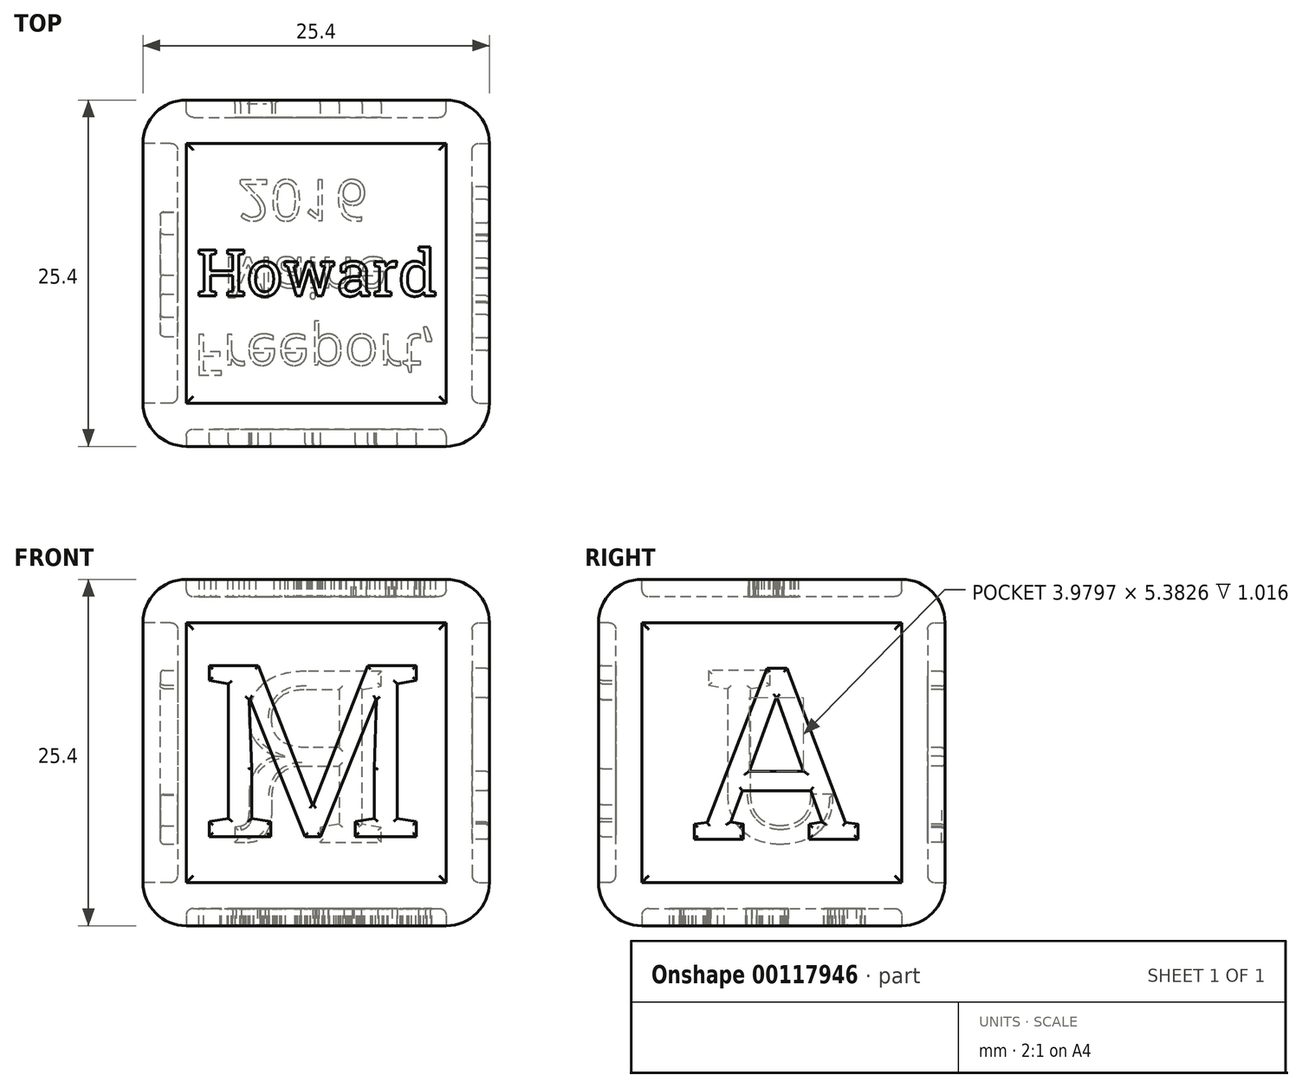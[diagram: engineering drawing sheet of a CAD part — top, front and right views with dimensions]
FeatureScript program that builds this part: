
annotation { "Feature Type Name" : "Feature", "Feature Type Description" : "" }
export const myFeature = defineFeature(function(context is Context, id is Id, definition is map)
    precondition{}
    {
        {
            var Q0;
            Q0=qCreatedBy(makeId("Top.planeOp"),FACE);
            var sketch = newSketch(context, id + "F0", { "sketchPlane" : qUnion([Q0])});
            skLineSegment(sketch, "E0.bottom", {"start": v(12.7, -12.7) * mm, "end": v(-12.7, -12.7) * mm});
            skLineSegment(sketch, "E0.top", {"start": v(12.7, 12.7) * mm, "end": v(-12.7, 12.7) * mm});
            skLineSegment(sketch, "E0.left", {"start": v(12.7, -12.7) * mm, "end": v(12.7, 12.7) * mm});
            skLineSegment(sketch, "E0.right", {"start": v(-12.7, -12.7) * mm, "end": v(-12.7, 12.7) * mm});
            skPoint(sketch, "E0.middle", {"position": v(0, 0) * mm});
            skSolve(sketch);
        }
        {
            var Q0;
            Q0=makeQuery(id+"F0.imprint","IMPRINT",FACE,{"disambiguationData":[TD([[makeQuery(id+"F0.imprint","IMPRINT",EDGE,{"derivedFrom":sQuery(id+"F0.wireOp",EDGE,"E0.bottom")}),-1.0]])]});
            extrude(context, id + "F1", {"entities" : qUnion([Q0]), "depth" : 25.4 * mm});
        }
        {
            var Q0;
            Q0=makeQuery(id+"F1.opExtrude","CAP_FACE",FACE,{"disambiguationData":[OSD([sQuery(id+"F0.wireOp",EDGE,"E0.bottom"),sQuery(id+"F0.wireOp",EDGE,"E0.top"),sQuery(id+"F0.wireOp",EDGE,"E0.left"),sQuery(id+"F0.wireOp",EDGE,"E0.right")])],"isStart":false});
            var Q1;
            Q1=makeQuery(id+"F1.opExtrude","SWEPT_FACE",FACE,{"disambiguationData":[OSD([sQuery(id+"F0.wireOp",EDGE,"E0.bottom")])]});
            var Q2;
            Q2=makeQuery(id+"F1.opExtrude","SWEPT_FACE",FACE,{"disambiguationData":[OSD([sQuery(id+"F0.wireOp",EDGE,"E0.left")])]});
            var Q3;
            Q3=makeQuery(id+"F1.opExtrude","CAP_FACE",FACE,{"disambiguationData":[OSD([sQuery(id+"F0.wireOp",EDGE,"E0.bottom"),sQuery(id+"F0.wireOp",EDGE,"E0.top"),sQuery(id+"F0.wireOp",EDGE,"E0.left"),sQuery(id+"F0.wireOp",EDGE,"E0.right")])],"isStart":true});
            var Q4;
            Q4=makeQuery(id+"F1.opExtrude","SWEPT_FACE",FACE,{"disambiguationData":[OSD([sQuery(id+"F0.wireOp",EDGE,"E0.right")])]});
            fillet(context, id + "F2", {"entities" : qUnion([Q0, Q1, Q2, Q3, Q4]), "radius" : 3.17 * mm, "tangentPropagation" : true, "allowEdgeOverflow" : false});
        }
        {
            var Q0;
            Q0=makeQuery(id+"F1.opExtrude","SWEPT_FACE",FACE,{"disambiguationData":[OSD([sQuery(id+"F0.wireOp",EDGE,"E0.bottom")])]});
            var sketch = newSketch(context, id + "F3", { "sketchPlane" : qUnion([Q0])});
            skPoint(sketch, "E1", {"position": v(0, 22.23) * mm});
            skLineSegment(sketch, "E2", {"start": v(0, 22.23) * mm, "end": v(0, 3.18) * mm, "construction": true});
            skLineSegment(sketch, "E3", {"start": v(9.53, 12.7) * mm, "end": v(-9.53, 12.7) * mm, "construction": true});
            skPoint(sketch, "E4", {"position": v(0, 12.7) * mm});
            skSolve(sketch);
        }
        {
            var Q0;
            {var subQ0=sQuery(id+"F0.wireOp",EDGE,"E0.bottom");var subQ1=makeQuery(id+"F1.opExtrude","SWEPT_FACE",FACE,{"disambiguationData":[OSD([subQ0])]});Q0=makeQuery(id+"F3.imprint","IMPRINT",FACE,{"disambiguationData":[TD([[makeQuery(id+"F3.imprint","IMPRINT",EDGE,{"derivedFrom":makeQuery(id+"F2.opFillet","BLEND_EDGE",EDGE,{"blendedFrom":[makeQuery(id+"F1.opExtrude","CAP_EDGE",EDGE,{"disambiguationData":[OSD([subQ0])],"isStart":true}),subQ1],"blendedInto":[subQ1]})}),1.0]])]});}
            extrude(context, id + "F4", {"entities" : qUnion([Q0]), "operationType" : NewBodyOperationType.REMOVE, "oppositeDirection" : true, "depth" : 1.27 * mm});
        }
        {
            var Q0;
            Q0=makeQuery(id+"F1.opExtrude","SWEPT_FACE",FACE,{"disambiguationData":[OSD([sQuery(id+"F0.wireOp",EDGE,"E0.left")])]});
            extrude(context, id + "F5", {"entities" : qUnion([Q0]), "operationType" : NewBodyOperationType.REMOVE, "oppositeDirection" : true, "depth" : 1.27 * mm});
        }
        {
            var Q0;
            Q0=makeQuery(id+"F1.opExtrude","SWEPT_FACE",FACE,{"disambiguationData":[OSD([sQuery(id+"F0.wireOp",EDGE,"E0.right")])]});
            extrude(context, id + "F6", {"entities" : qUnion([Q0]), "operationType" : NewBodyOperationType.REMOVE, "oppositeDirection" : true, "depth" : 2.54 * mm});
        }
        {
            var Q0;
            Q0=makeQuery(id+"F1.opExtrude","SWEPT_FACE",FACE,{"disambiguationData":[OSD([sQuery(id+"F0.wireOp",EDGE,"E0.top")])]});
            extrude(context, id + "F7", {"entities" : qUnion([Q0]), "operationType" : NewBodyOperationType.REMOVE, "oppositeDirection" : true, "depth" : 1.27 * mm});
        }
        {
            var Q0;
            Q0=makeQuery(id+"F1.opExtrude","CAP_FACE",FACE,{"disambiguationData":[OSD([sQuery(id+"F0.wireOp",EDGE,"E0.bottom"),sQuery(id+"F0.wireOp",EDGE,"E0.top"),sQuery(id+"F0.wireOp",EDGE,"E0.left"),sQuery(id+"F0.wireOp",EDGE,"E0.right")])],"isStart":true});
            extrude(context, id + "F8", {"entities" : qUnion([Q0]), "operationType" : NewBodyOperationType.REMOVE, "oppositeDirection" : true, "depth" : 1.27 * mm});
        }
        {
            var Q0;
            Q0=makeQuery(id+"F1.opExtrude","CAP_FACE",FACE,{"disambiguationData":[OSD([sQuery(id+"F0.wireOp",EDGE,"E0.bottom"),sQuery(id+"F0.wireOp",EDGE,"E0.top"),sQuery(id+"F0.wireOp",EDGE,"E0.left"),sQuery(id+"F0.wireOp",EDGE,"E0.right")])],"isStart":false});
            extrude(context, id + "F9", {"entities" : qUnion([Q0]), "operationType" : NewBodyOperationType.REMOVE, "oppositeDirection" : true, "depth" : 1.27 * mm});
        }
        {
            var Q0;
            {var subQ0=sQuery(id+"F0.wireOp",EDGE,"E0.right");Q0=makeQuery(id+"F6.boolean.opBoolean","COPY",EDGE,{"derivedFrom":makeQuery(id+"F6.opExtrude","CAP_EDGE",EDGE,{"disambiguationData":[OSD([subQ0]),TDD([makeQuery(id+"F2.opFillet","BLEND_EDGE",EDGE,{"blendedFrom":[makeQuery(id+"F1.opExtrude","CAP_EDGE",EDGE,{"disambiguationData":[OSD([subQ0])],"isStart":true}),makeQuery(id+"F1.opExtrude","SWEPT_FACE",FACE,{"disambiguationData":[OSD([subQ0])]})],"blendedInto":[makeQuery(id+"F1.opExtrude","SWEPT_FACE",FACE,{"disambiguationData":[OSD([subQ0])]})]})])],"isStart":false})});}
            var Q1;
            Q1=makeQuery(id+"F6.boolean.opBoolean","COPY",EDGE,{"derivedFrom":makeQuery(id+"F6.opExtrude","CAP_EDGE",EDGE,{"disambiguationData":[OSD([sQuery(id+"F0.wireOp",EDGE,"E0.bottom"),sQuery(id+"F0.wireOp",EDGE,"E0.right")])],"isStart":false})});
            var Q2;
            {var subQ0=sQuery(id+"F0.wireOp",EDGE,"E0.right");Q2=makeQuery(id+"F6.boolean.opBoolean","COPY",EDGE,{"derivedFrom":makeQuery(id+"F6.opExtrude","CAP_EDGE",EDGE,{"disambiguationData":[OSD([subQ0]),TDD([makeQuery(id+"F2.opFillet","BLEND_EDGE",EDGE,{"blendedFrom":[makeQuery(id+"F1.opExtrude","CAP_EDGE",EDGE,{"disambiguationData":[OSD([subQ0])],"isStart":false}),makeQuery(id+"F1.opExtrude","SWEPT_FACE",FACE,{"disambiguationData":[OSD([subQ0])]})],"blendedInto":[makeQuery(id+"F1.opExtrude","SWEPT_FACE",FACE,{"disambiguationData":[OSD([subQ0])]})]})])],"isStart":false})});}
            var Q3;
            Q3=makeQuery(id+"F6.boolean.opBoolean","COPY",EDGE,{"derivedFrom":makeQuery(id+"F6.opExtrude","CAP_EDGE",EDGE,{"disambiguationData":[OSD([sQuery(id+"F0.wireOp",EDGE,"E0.top"),sQuery(id+"F0.wireOp",EDGE,"E0.right")])],"isStart":false})});
            var Q4;
            Q4=makeQuery(id+"F4.boolean.opBoolean","COPY",EDGE,{"derivedFrom":makeQuery(id+"F4.opExtrude","CAP_EDGE",EDGE,{"disambiguationData":[OSD([sQuery(id+"F0.wireOp",EDGE,"E0.bottom"),sQuery(id+"F0.wireOp",EDGE,"E0.right")])],"isStart":false})});
            var Q5;
            {var subQ0=sQuery(id+"F0.wireOp",EDGE,"E0.bottom");Q5=makeQuery(id+"F4.boolean.opBoolean","COPY",EDGE,{"derivedFrom":makeQuery(id+"F4.opExtrude","CAP_EDGE",EDGE,{"disambiguationData":[OSD([subQ0]),TDD([makeQuery(id+"F3.imprint","IMPRINT",EDGE,{"derivedFrom":makeQuery(id+"F2.opFillet","BLEND_EDGE",EDGE,{"blendedFrom":[makeQuery(id+"F1.opExtrude","CAP_EDGE",EDGE,{"disambiguationData":[OSD([subQ0])],"isStart":true}),makeQuery(id+"F1.opExtrude","SWEPT_FACE",FACE,{"disambiguationData":[OSD([subQ0])]})],"blendedInto":[makeQuery(id+"F1.opExtrude","SWEPT_FACE",FACE,{"disambiguationData":[OSD([subQ0])]})]})})])],"isStart":false})});}
            var Q6;
            {var subQ0=sQuery(id+"F0.wireOp",EDGE,"E0.bottom");Q6=makeQuery(id+"F4.boolean.opBoolean","COPY",EDGE,{"derivedFrom":makeQuery(id+"F4.opExtrude","CAP_EDGE",EDGE,{"disambiguationData":[OSD([subQ0]),TDD([makeQuery(id+"F3.imprint","IMPRINT",EDGE,{"derivedFrom":makeQuery(id+"F2.opFillet","BLEND_EDGE",EDGE,{"blendedFrom":[makeQuery(id+"F1.opExtrude","CAP_EDGE",EDGE,{"disambiguationData":[OSD([subQ0])],"isStart":false}),makeQuery(id+"F1.opExtrude","SWEPT_FACE",FACE,{"disambiguationData":[OSD([subQ0])]})],"blendedInto":[makeQuery(id+"F1.opExtrude","SWEPT_FACE",FACE,{"disambiguationData":[OSD([subQ0])]})]})})])],"isStart":false})});}
            var Q7;
            Q7=makeQuery(id+"F4.boolean.opBoolean","COPY",EDGE,{"derivedFrom":makeQuery(id+"F4.opExtrude","CAP_EDGE",EDGE,{"disambiguationData":[OSD([sQuery(id+"F0.wireOp",EDGE,"E0.bottom"),sQuery(id+"F0.wireOp",EDGE,"E0.left")])],"isStart":false})});
            var Q8;
            {var subQ0=sQuery(id+"F0.wireOp",EDGE,"E0.left");Q8=makeQuery(id+"F5.boolean.opBoolean","COPY",EDGE,{"derivedFrom":makeQuery(id+"F5.opExtrude","CAP_EDGE",EDGE,{"disambiguationData":[OSD([subQ0]),TDD([makeQuery(id+"F2.opFillet","BLEND_EDGE",EDGE,{"blendedFrom":[makeQuery(id+"F1.opExtrude","CAP_EDGE",EDGE,{"disambiguationData":[OSD([subQ0])],"isStart":false}),makeQuery(id+"F1.opExtrude","SWEPT_FACE",FACE,{"disambiguationData":[OSD([subQ0])]})],"blendedInto":[makeQuery(id+"F1.opExtrude","SWEPT_FACE",FACE,{"disambiguationData":[OSD([subQ0])]})]})])],"isStart":false})});}
            var Q9;
            Q9=makeQuery(id+"F5.boolean.opBoolean","COPY",EDGE,{"derivedFrom":makeQuery(id+"F5.opExtrude","CAP_EDGE",EDGE,{"disambiguationData":[OSD([sQuery(id+"F0.wireOp",EDGE,"E0.top"),sQuery(id+"F0.wireOp",EDGE,"E0.left")])],"isStart":false})});
            var Q10;
            Q10=makeQuery(id+"F5.boolean.opBoolean","COPY",EDGE,{"derivedFrom":makeQuery(id+"F5.opExtrude","CAP_EDGE",EDGE,{"disambiguationData":[OSD([sQuery(id+"F0.wireOp",EDGE,"E0.bottom"),sQuery(id+"F0.wireOp",EDGE,"E0.left")])],"isStart":false})});
            var Q11;
            {var subQ0=sQuery(id+"F0.wireOp",EDGE,"E0.left");Q11=makeQuery(id+"F5.boolean.opBoolean","COPY",EDGE,{"derivedFrom":makeQuery(id+"F5.opExtrude","CAP_EDGE",EDGE,{"disambiguationData":[OSD([subQ0]),TDD([makeQuery(id+"F2.opFillet","BLEND_EDGE",EDGE,{"blendedFrom":[makeQuery(id+"F1.opExtrude","CAP_EDGE",EDGE,{"disambiguationData":[OSD([subQ0])],"isStart":true}),makeQuery(id+"F1.opExtrude","SWEPT_FACE",FACE,{"disambiguationData":[OSD([subQ0])]})],"blendedInto":[makeQuery(id+"F1.opExtrude","SWEPT_FACE",FACE,{"disambiguationData":[OSD([subQ0])]})]})])],"isStart":false})});}
            var Q12;
            {var subQ0=sQuery(id+"F0.wireOp",EDGE,"E0.top");Q12=makeQuery(id+"F7.boolean.opBoolean","COPY",EDGE,{"derivedFrom":makeQuery(id+"F7.opExtrude","CAP_EDGE",EDGE,{"disambiguationData":[OSD([subQ0]),TDD([makeQuery(id+"F2.opFillet","BLEND_EDGE",EDGE,{"blendedFrom":[makeQuery(id+"F1.opExtrude","CAP_EDGE",EDGE,{"disambiguationData":[OSD([subQ0])],"isStart":true}),makeQuery(id+"F1.opExtrude","SWEPT_FACE",FACE,{"disambiguationData":[OSD([subQ0])]})],"blendedInto":[makeQuery(id+"F1.opExtrude","SWEPT_FACE",FACE,{"disambiguationData":[OSD([subQ0])]})]})])],"isStart":false})});}
            var Q13;
            Q13=makeQuery(id+"F7.boolean.opBoolean","COPY",EDGE,{"derivedFrom":makeQuery(id+"F7.opExtrude","CAP_EDGE",EDGE,{"disambiguationData":[OSD([sQuery(id+"F0.wireOp",EDGE,"E0.top"),sQuery(id+"F0.wireOp",EDGE,"E0.right")])],"isStart":false})});
            var Q14;
            {var subQ0=sQuery(id+"F0.wireOp",EDGE,"E0.top");Q14=makeQuery(id+"F7.boolean.opBoolean","COPY",EDGE,{"derivedFrom":makeQuery(id+"F7.opExtrude","CAP_EDGE",EDGE,{"disambiguationData":[OSD([subQ0]),TDD([makeQuery(id+"F2.opFillet","BLEND_EDGE",EDGE,{"blendedFrom":[makeQuery(id+"F1.opExtrude","CAP_EDGE",EDGE,{"disambiguationData":[OSD([subQ0])],"isStart":false}),makeQuery(id+"F1.opExtrude","SWEPT_FACE",FACE,{"disambiguationData":[OSD([subQ0])]})],"blendedInto":[makeQuery(id+"F1.opExtrude","SWEPT_FACE",FACE,{"disambiguationData":[OSD([subQ0])]})]})])],"isStart":false})});}
            var Q15;
            Q15=makeQuery(id+"F7.boolean.opBoolean","COPY",EDGE,{"derivedFrom":makeQuery(id+"F7.opExtrude","CAP_EDGE",EDGE,{"disambiguationData":[OSD([sQuery(id+"F0.wireOp",EDGE,"E0.top"),sQuery(id+"F0.wireOp",EDGE,"E0.left")])],"isStart":false})});
            var Q16;
            {var subQ0=sQuery(id+"F0.wireOp",EDGE,"E0.right");var subQ1=sQuery(id+"F0.wireOp",EDGE,"E0.left");var subQ2=sQuery(id+"F0.wireOp",EDGE,"E0.top");var subQ3=sQuery(id+"F0.wireOp",EDGE,"E0.bottom");Q16=makeQuery(id+"F9.boolean.opBoolean","COPY",EDGE,{"derivedFrom":makeQuery(id+"F9.opExtrude","CAP_EDGE",EDGE,{"disambiguationData":[OSD([subQ3,subQ2,subQ1,subQ0]),TDD([makeQuery(id+"F2.opFillet","BLEND_EDGE",EDGE,{"blendedFrom":[makeQuery(id+"F1.opExtrude","CAP_EDGE",EDGE,{"disambiguationData":[OSD([subQ2])],"isStart":false}),makeQuery(id+"F1.opExtrude","CAP_FACE",FACE,{"disambiguationData":[OSD([subQ3,subQ2,subQ1,subQ0])],"isStart":false})],"blendedInto":[makeQuery(id+"F1.opExtrude","CAP_FACE",FACE,{"disambiguationData":[OSD([subQ3,subQ2,subQ1,subQ0])],"isStart":false})]})])],"isStart":false})});}
            var Q17;
            {var subQ0=sQuery(id+"F0.wireOp",EDGE,"E0.right");var subQ1=sQuery(id+"F0.wireOp",EDGE,"E0.left");var subQ2=sQuery(id+"F0.wireOp",EDGE,"E0.top");var subQ3=sQuery(id+"F0.wireOp",EDGE,"E0.bottom");Q17=makeQuery(id+"F9.boolean.opBoolean","COPY",EDGE,{"derivedFrom":makeQuery(id+"F9.opExtrude","CAP_EDGE",EDGE,{"disambiguationData":[OSD([subQ3,subQ2,subQ1,subQ0]),TDD([makeQuery(id+"F2.opFillet","BLEND_EDGE",EDGE,{"blendedFrom":[makeQuery(id+"F1.opExtrude","CAP_EDGE",EDGE,{"disambiguationData":[OSD([subQ1])],"isStart":false}),makeQuery(id+"F1.opExtrude","CAP_FACE",FACE,{"disambiguationData":[OSD([subQ3,subQ2,subQ1,subQ0])],"isStart":false})],"blendedInto":[makeQuery(id+"F1.opExtrude","CAP_FACE",FACE,{"disambiguationData":[OSD([subQ3,subQ2,subQ1,subQ0])],"isStart":false})]})])],"isStart":false})});}
            var Q18;
            {var subQ0=sQuery(id+"F0.wireOp",EDGE,"E0.right");var subQ1=sQuery(id+"F0.wireOp",EDGE,"E0.left");var subQ2=sQuery(id+"F0.wireOp",EDGE,"E0.top");var subQ3=sQuery(id+"F0.wireOp",EDGE,"E0.bottom");Q18=makeQuery(id+"F9.boolean.opBoolean","COPY",EDGE,{"derivedFrom":makeQuery(id+"F9.opExtrude","CAP_EDGE",EDGE,{"disambiguationData":[OSD([subQ3,subQ2,subQ1,subQ0]),TDD([makeQuery(id+"F2.opFillet","BLEND_EDGE",EDGE,{"blendedFrom":[makeQuery(id+"F1.opExtrude","CAP_EDGE",EDGE,{"disambiguationData":[OSD([subQ3])],"isStart":false}),makeQuery(id+"F1.opExtrude","CAP_FACE",FACE,{"disambiguationData":[OSD([subQ3,subQ2,subQ1,subQ0])],"isStart":false})],"blendedInto":[makeQuery(id+"F1.opExtrude","CAP_FACE",FACE,{"disambiguationData":[OSD([subQ3,subQ2,subQ1,subQ0])],"isStart":false})]})])],"isStart":false})});}
            var Q19;
            {var subQ0=sQuery(id+"F0.wireOp",EDGE,"E0.right");var subQ1=sQuery(id+"F0.wireOp",EDGE,"E0.left");var subQ2=sQuery(id+"F0.wireOp",EDGE,"E0.top");var subQ3=sQuery(id+"F0.wireOp",EDGE,"E0.bottom");Q19=makeQuery(id+"F9.boolean.opBoolean","COPY",EDGE,{"derivedFrom":makeQuery(id+"F9.opExtrude","CAP_EDGE",EDGE,{"disambiguationData":[OSD([subQ3,subQ2,subQ1,subQ0]),TDD([makeQuery(id+"F2.opFillet","BLEND_EDGE",EDGE,{"blendedFrom":[makeQuery(id+"F1.opExtrude","CAP_EDGE",EDGE,{"disambiguationData":[OSD([subQ0])],"isStart":false}),makeQuery(id+"F1.opExtrude","CAP_FACE",FACE,{"disambiguationData":[OSD([subQ3,subQ2,subQ1,subQ0])],"isStart":false})],"blendedInto":[makeQuery(id+"F1.opExtrude","CAP_FACE",FACE,{"disambiguationData":[OSD([subQ3,subQ2,subQ1,subQ0])],"isStart":false})]})])],"isStart":false})});}
            var Q20;
            {var subQ0=sQuery(id+"F0.wireOp",EDGE,"E0.right");var subQ1=sQuery(id+"F0.wireOp",EDGE,"E0.left");var subQ2=sQuery(id+"F0.wireOp",EDGE,"E0.top");var subQ3=sQuery(id+"F0.wireOp",EDGE,"E0.bottom");Q20=makeQuery(id+"F8.boolean.opBoolean","COPY",EDGE,{"derivedFrom":makeQuery(id+"F8.opExtrude","CAP_EDGE",EDGE,{"disambiguationData":[OSD([subQ3,subQ2,subQ1,subQ0]),TDD([makeQuery(id+"F2.opFillet","BLEND_EDGE",EDGE,{"blendedFrom":[makeQuery(id+"F1.opExtrude","CAP_EDGE",EDGE,{"disambiguationData":[OSD([subQ3])],"isStart":true}),makeQuery(id+"F1.opExtrude","CAP_FACE",FACE,{"disambiguationData":[OSD([subQ3,subQ2,subQ1,subQ0])],"isStart":true})],"blendedInto":[makeQuery(id+"F1.opExtrude","CAP_FACE",FACE,{"disambiguationData":[OSD([subQ3,subQ2,subQ1,subQ0])],"isStart":true})]})])],"isStart":false})});}
            var Q21;
            {var subQ0=sQuery(id+"F0.wireOp",EDGE,"E0.right");var subQ1=sQuery(id+"F0.wireOp",EDGE,"E0.left");var subQ2=sQuery(id+"F0.wireOp",EDGE,"E0.top");var subQ3=sQuery(id+"F0.wireOp",EDGE,"E0.bottom");Q21=makeQuery(id+"F8.boolean.opBoolean","COPY",EDGE,{"derivedFrom":makeQuery(id+"F8.opExtrude","CAP_EDGE",EDGE,{"disambiguationData":[OSD([subQ3,subQ2,subQ1,subQ0]),TDD([makeQuery(id+"F2.opFillet","BLEND_EDGE",EDGE,{"blendedFrom":[makeQuery(id+"F1.opExtrude","CAP_EDGE",EDGE,{"disambiguationData":[OSD([subQ0])],"isStart":true}),makeQuery(id+"F1.opExtrude","CAP_FACE",FACE,{"disambiguationData":[OSD([subQ3,subQ2,subQ1,subQ0])],"isStart":true})],"blendedInto":[makeQuery(id+"F1.opExtrude","CAP_FACE",FACE,{"disambiguationData":[OSD([subQ3,subQ2,subQ1,subQ0])],"isStart":true})]})])],"isStart":false})});}
            var Q22;
            {var subQ0=sQuery(id+"F0.wireOp",EDGE,"E0.right");var subQ1=sQuery(id+"F0.wireOp",EDGE,"E0.left");var subQ2=sQuery(id+"F0.wireOp",EDGE,"E0.top");var subQ3=sQuery(id+"F0.wireOp",EDGE,"E0.bottom");Q22=makeQuery(id+"F8.boolean.opBoolean","COPY",EDGE,{"derivedFrom":makeQuery(id+"F8.opExtrude","CAP_EDGE",EDGE,{"disambiguationData":[OSD([subQ3,subQ2,subQ1,subQ0]),TDD([makeQuery(id+"F2.opFillet","BLEND_EDGE",EDGE,{"blendedFrom":[makeQuery(id+"F1.opExtrude","CAP_EDGE",EDGE,{"disambiguationData":[OSD([subQ1])],"isStart":true}),makeQuery(id+"F1.opExtrude","CAP_FACE",FACE,{"disambiguationData":[OSD([subQ3,subQ2,subQ1,subQ0])],"isStart":true})],"blendedInto":[makeQuery(id+"F1.opExtrude","CAP_FACE",FACE,{"disambiguationData":[OSD([subQ3,subQ2,subQ1,subQ0])],"isStart":true})]})])],"isStart":false})});}
            var Q23;
            {var subQ0=sQuery(id+"F0.wireOp",EDGE,"E0.right");var subQ1=sQuery(id+"F0.wireOp",EDGE,"E0.left");var subQ2=sQuery(id+"F0.wireOp",EDGE,"E0.top");var subQ3=sQuery(id+"F0.wireOp",EDGE,"E0.bottom");Q23=makeQuery(id+"F8.boolean.opBoolean","COPY",EDGE,{"derivedFrom":makeQuery(id+"F8.opExtrude","CAP_EDGE",EDGE,{"disambiguationData":[OSD([subQ3,subQ2,subQ1,subQ0]),TDD([makeQuery(id+"F2.opFillet","BLEND_EDGE",EDGE,{"blendedFrom":[makeQuery(id+"F1.opExtrude","CAP_EDGE",EDGE,{"disambiguationData":[OSD([subQ2])],"isStart":true}),makeQuery(id+"F1.opExtrude","CAP_FACE",FACE,{"disambiguationData":[OSD([subQ3,subQ2,subQ1,subQ0])],"isStart":true})],"blendedInto":[makeQuery(id+"F1.opExtrude","CAP_FACE",FACE,{"disambiguationData":[OSD([subQ3,subQ2,subQ1,subQ0])],"isStart":true})]})])],"isStart":false})});}
            fillet(context, id + "F10", {"entities" : qUnion([Q0, Q1, Q2, Q3, Q4, Q5, Q6, Q7, Q8, Q9, Q10, Q11, Q12, Q13, Q14, Q15, Q16, Q17, Q18, Q19, Q20, Q21, Q22, Q23]), "radius" : 0.5 * mm, "tangentPropagation" : true, "allowEdgeOverflow" : false});
        }
        {
            var Q0;
            Q0=makeQuery(id+"F4.boolean.opBoolean","COPY",FACE,{"derivedFrom":makeQuery(id+"F4.opExtrude","CAP_FACE",FACE,{"disambiguationData":[OSD([sQuery(id+"F0.wireOp",EDGE,"E0.bottom"),sQuery(id+"F0.wireOp",EDGE,"E0.left"),sQuery(id+"F0.wireOp",EDGE,"E0.right")])],"isStart":false})});
            var sketch = newSketch(context, id + "F11", { "sketchPlane" : qUnion([Q0])});
            skText(sketch, "E5", { "text": "M", "fontName": "RobotoSlab-Regular.ttf"});
            const initialGuessF11  = {"E5": [-0.00845, 0.00654, 1, 0, 0.0127]};
            skSetInitialGuess(sketch, initialGuessF11);
            skSolve(sketch);
        }
        {
            var Q0;
            Q0=makeQuery(id+"F5.boolean.opBoolean","COPY",FACE,{"derivedFrom":makeQuery(id+"F5.opExtrude","CAP_FACE",FACE,{"disambiguationData":[OSD([sQuery(id+"F0.wireOp",EDGE,"E0.left")])],"isStart":false})});
            var sketch = newSketch(context, id + "F12", { "sketchPlane" : qUnion([Q0])});
            skText(sketch, "E6", { "text": "A", "fontName": "RobotoSlab-Regular.ttf"});
            const initialGuessF12  = {"E6": [-0.00614, 0.00635, 1, 0, 0.0127]};
            skSetInitialGuess(sketch, initialGuessF12);
            skSolve(sketch);
        }
        {
            var Q0;
            Q0=makeQuery(id+"F7.boolean.opBoolean","COPY",FACE,{"derivedFrom":makeQuery(id+"F7.opExtrude","CAP_FACE",FACE,{"disambiguationData":[OSD([sQuery(id+"F0.wireOp",EDGE,"E0.top")])],"isStart":false})});
            var sketch = newSketch(context, id + "F13", { "sketchPlane" : qUnion([Q0])});
            skText(sketch, "E7", { "text": "R", "fontName": "RobotoSlab-Regular.ttf"});
            const initialGuessF13  = {"E7": [-0.00539, 0.00612, 1, 0, 0.0127]};
            skSetInitialGuess(sketch, initialGuessF13);
            skSolve(sketch);
        }
        {
            var Q0;
            Q0=makeQuery(id+"F6.boolean.opBoolean","COPY",FACE,{"derivedFrom":makeQuery(id+"F6.opExtrude","CAP_FACE",FACE,{"disambiguationData":[OSD([sQuery(id+"F0.wireOp",EDGE,"E0.right")])],"isStart":false})});
            var sketch = newSketch(context, id + "F14", { "sketchPlane" : qUnion([Q0])});
            skText(sketch, "E8", { "text": "J", "fontName": "RobotoSlab-Regular.ttf"});
            const initialGuessF14  = {"E8": [-0.00504, 0.00618, 1, 0, 0.0127]};
            skSetInitialGuess(sketch, initialGuessF14);
            skSolve(sketch);
        }
        {
            var Q0;
            Q0=makeQuery(id+"F9.boolean.opBoolean","COPY",FACE,{"derivedFrom":makeQuery(id+"F9.opExtrude","CAP_FACE",FACE,{"disambiguationData":[OSD([sQuery(id+"F0.wireOp",EDGE,"E0.bottom"),sQuery(id+"F0.wireOp",EDGE,"E0.top"),sQuery(id+"F0.wireOp",EDGE,"E0.left"),sQuery(id+"F0.wireOp",EDGE,"E0.right")])],"isStart":false})});
            var sketch = newSketch(context, id + "F15", { "sketchPlane" : qUnion([Q0])});
            skText(sketch, "E9", { "text": "Howard", "fontName": "RobotoSlab-Regular.ttf"});
            const initialGuessF15  = {"E9": [-0.00875, -0.00167, 1, 0, 0.00341]};
            skSetInitialGuess(sketch, initialGuessF15);
            skSolve(sketch);
        }
        {
            var Q0;
            Q0=makeQuery(id+"F8.boolean.opBoolean","COPY",FACE,{"derivedFrom":makeQuery(id+"F8.opExtrude","CAP_FACE",FACE,{"disambiguationData":[OSD([sQuery(id+"F0.wireOp",EDGE,"E0.bottom"),sQuery(id+"F0.wireOp",EDGE,"E0.top"),sQuery(id+"F0.wireOp",EDGE,"E0.left"),sQuery(id+"F0.wireOp",EDGE,"E0.right")])],"isStart":false})});
            var sketch = newSketch(context, id + "F16", { "sketchPlane" : qUnion([Q0])});
            skText(sketch, "E10", { "text": "Freeport,\n  Maine\n   2016", "fontName": "OpenSans-Regular.ttf"});
            const initialGuessF16  = {"E10": [-0.00902, 0.0045, 1, 0, 0.003]};
            skSetInitialGuess(sketch, initialGuessF16);
            skSolve(sketch);
        }
        {
            var Q0;
            Q0 = qSketchRegion(id + "F11", true);
            extrude(context, id + "F17", {"entities" : qUnion([Q0]), "operationType" : NewBodyOperationType.ADD, "depth" : 1.27 * mm});
        }
        {
            var Q0;
            Q0 = qSketchRegion(id + "F12", true);
            extrude(context, id + "F18", {"entities" : qUnion([Q0]), "operationType" : NewBodyOperationType.ADD, "depth" : 1.27 * mm});
        }
        {
            var Q0;
            Q0 = qSketchRegion(id + "F13", true);
            extrude(context, id + "F19", {"entities" : qUnion([Q0]), "operationType" : NewBodyOperationType.ADD, "depth" : 1.27 * mm});
        }
        {
            var Q0;
            Q0 = qSketchRegion(id + "F14", true);
            extrude(context, id + "F20", {"entities" : qUnion([Q0]), "operationType" : NewBodyOperationType.ADD, "depth" : 1.27 * mm});
        }
        {
            var Q0;
            Q0 = qSketchRegion(id + "F15", true);
            extrude(context, id + "F21", {"entities" : qUnion([Q0]), "operationType" : NewBodyOperationType.ADD, "depth" : 1.27 * mm});
        }
        {
            var Q0;
            Q0 = qSketchRegion(id + "F16", true);
            extrude(context, id + "F22", {"entities" : qUnion([Q0]), "operationType" : NewBodyOperationType.ADD, "depth" : 1.27 * mm});
        }
        {
            var Q0;
            Q0=makeQuery(id+"F17.opExtrude","CAP_FACE",FACE,{"disambiguationData":[OSD([sQuery(id+"F11.wireOp",EDGE,"E5.sketch_text.stroke-0"),sQuery(id+"F11.wireOp",EDGE,"E5.sketch_text.stroke-1"),sQuery(id+"F11.wireOp",EDGE,"E5.sketch_text.stroke-2"),sQuery(id+"F11.wireOp",EDGE,"E5.sketch_text.stroke-3"),sQuery(id+"F11.wireOp",EDGE,"E5.sketch_text.stroke-4"),sQuery(id+"F11.wireOp",EDGE,"E5.sketch_text.stroke-5"),sQuery(id+"F11.wireOp",EDGE,"E5.sketch_text.stroke-6"),sQuery(id+"F11.wireOp",EDGE,"E5.sketch_text.stroke-7"),sQuery(id+"F11.wireOp",EDGE,"E5.sketch_text.stroke-8"),sQuery(id+"F11.wireOp",EDGE,"E5.sketch_text.stroke-9"),sQuery(id+"F11.wireOp",EDGE,"E5.sketch_text.stroke-10"),sQuery(id+"F11.wireOp",EDGE,"E5.sketch_text.stroke-11"),sQuery(id+"F11.wireOp",EDGE,"E5.sketch_text.stroke-12"),sQuery(id+"F11.wireOp",EDGE,"E5.sketch_text.stroke-13"),sQuery(id+"F11.wireOp",EDGE,"E5.sketch_text.stroke-14"),sQuery(id+"F11.wireOp",EDGE,"E5.sketch_text.stroke-15"),sQuery(id+"F11.wireOp",EDGE,"E5.sketch_text.stroke-16"),sQuery(id+"F11.wireOp",EDGE,"E5.sketch_text.stroke-17"),sQuery(id+"F11.wireOp",EDGE,"E5.sketch_text.stroke-18"),sQuery(id+"F11.wireOp",EDGE,"E5.sketch_text.stroke-19"),sQuery(id+"F11.wireOp",EDGE,"E5.sketch_text.stroke-20"),sQuery(id+"F11.wireOp",EDGE,"E5.sketch_text.stroke-21"),sQuery(id+"F11.wireOp",EDGE,"E5.sketch_text.stroke-22"),sQuery(id+"F11.wireOp",EDGE,"E5.sketch_text.stroke-23"),sQuery(id+"F11.wireOp",EDGE,"E5.sketch_text.stroke-24"),sQuery(id+"F11.wireOp",EDGE,"E5.sketch_text.stroke-25"),sQuery(id+"F11.wireOp",EDGE,"E5.sketch_text.stroke-26"),sQuery(id+"F11.wireOp",EDGE,"E5.sketch_text.stroke-27"),sQuery(id+"F11.wireOp",EDGE,"E5.sketch_text.stroke-28"),sQuery(id+"F11.wireOp",EDGE,"E5.sketch_text.stroke-29"),sQuery(id+"F11.wireOp",EDGE,"E5.sketch_text.stroke-30")])],"isStart":false});
            var Q1;
            Q1=makeQuery(id+"F18.opExtrude","CAP_FACE",FACE,{"disambiguationData":[OSD([sQuery(id+"F12.wireOp",EDGE,"E6.sketch_text.stroke-0"),sQuery(id+"F12.wireOp",EDGE,"E6.sketch_text.stroke-1"),sQuery(id+"F12.wireOp",EDGE,"E6.sketch_text.stroke-2"),sQuery(id+"F12.wireOp",EDGE,"E6.sketch_text.stroke-3"),sQuery(id+"F12.wireOp",EDGE,"E6.sketch_text.stroke-4"),sQuery(id+"F12.wireOp",EDGE,"E6.sketch_text.stroke-5"),sQuery(id+"F12.wireOp",EDGE,"E6.sketch_text.stroke-6"),sQuery(id+"F12.wireOp",EDGE,"E6.sketch_text.stroke-7"),sQuery(id+"F12.wireOp",EDGE,"E6.sketch_text.stroke-8"),sQuery(id+"F12.wireOp",EDGE,"E6.sketch_text.stroke-9"),sQuery(id+"F12.wireOp",EDGE,"E6.sketch_text.stroke-10"),sQuery(id+"F12.wireOp",EDGE,"E6.sketch_text.stroke-11"),sQuery(id+"F12.wireOp",EDGE,"E6.sketch_text.stroke-12"),sQuery(id+"F12.wireOp",EDGE,"E6.sketch_text.stroke-13"),sQuery(id+"F12.wireOp",EDGE,"E6.sketch_text.stroke-14"),sQuery(id+"F12.wireOp",EDGE,"E6.sketch_text.stroke-15"),sQuery(id+"F12.wireOp",EDGE,"E6.sketch_text.stroke-16"),sQuery(id+"F12.wireOp",EDGE,"E6.sketch_text.stroke-17"),sQuery(id+"F12.wireOp",EDGE,"E6.sketch_text.stroke-18"),sQuery(id+"F12.wireOp",EDGE,"E6.sketch_text.stroke-19")])],"isStart":false});
            var Q2;
            Q2=makeQuery(id+"F19.opExtrude","CAP_FACE",FACE,{"disambiguationData":[OSD([sQuery(id+"F13.wireOp",EDGE,"E7.sketch_text.stroke-0"),sQuery(id+"F13.wireOp",EDGE,"E7.sketch_text.stroke-1"),sQuery(id+"F13.wireOp",EDGE,"E7.sketch_text.stroke-2"),sQuery(id+"F13.wireOp",EDGE,"E7.sketch_text.stroke-3"),sQuery(id+"F13.wireOp",EDGE,"E7.sketch_text.stroke-4"),sQuery(id+"F13.wireOp",EDGE,"E7.sketch_text.stroke-5"),sQuery(id+"F13.wireOp",EDGE,"E7.sketch_text.stroke-6"),sQuery(id+"F13.wireOp",EDGE,"E7.sketch_text.stroke-7"),sQuery(id+"F13.wireOp",EDGE,"E7.sketch_text.stroke-8"),sQuery(id+"F13.wireOp",EDGE,"E7.sketch_text.stroke-9"),sQuery(id+"F13.wireOp",EDGE,"E7.sketch_text.stroke-10"),sQuery(id+"F13.wireOp",EDGE,"E7.sketch_text.stroke-11"),sQuery(id+"F13.wireOp",EDGE,"E7.sketch_text.stroke-12"),sQuery(id+"F13.wireOp",EDGE,"E7.sketch_text.stroke-13"),sQuery(id+"F13.wireOp",EDGE,"E7.sketch_text.stroke-14"),sQuery(id+"F13.wireOp",EDGE,"E7.sketch_text.stroke-15"),sQuery(id+"F13.wireOp",EDGE,"E7.sketch_text.stroke-16"),sQuery(id+"F13.wireOp",EDGE,"E7.sketch_text.stroke-17"),sQuery(id+"F13.wireOp",EDGE,"E7.sketch_text.stroke-18"),sQuery(id+"F13.wireOp",EDGE,"E7.sketch_text.stroke-19"),sQuery(id+"F13.wireOp",EDGE,"E7.sketch_text.stroke-20"),sQuery(id+"F13.wireOp",EDGE,"E7.sketch_text.stroke-21"),sQuery(id+"F13.wireOp",EDGE,"E7.sketch_text.stroke-22"),sQuery(id+"F13.wireOp",EDGE,"E7.sketch_text.stroke-23"),sQuery(id+"F13.wireOp",EDGE,"E7.sketch_text.stroke-24"),sQuery(id+"F13.wireOp",EDGE,"E7.sketch_text.stroke-25"),sQuery(id+"F13.wireOp",EDGE,"E7.sketch_text.stroke-26"),sQuery(id+"F13.wireOp",EDGE,"E7.sketch_text.stroke-27"),sQuery(id+"F13.wireOp",EDGE,"E7.sketch_text.stroke-28"),sQuery(id+"F13.wireOp",EDGE,"E7.sketch_text.stroke-29"),sQuery(id+"F13.wireOp",EDGE,"E7.sketch_text.stroke-30"),sQuery(id+"F13.wireOp",EDGE,"E7.sketch_text.stroke-31"),sQuery(id+"F13.wireOp",EDGE,"E7.sketch_text.stroke-32"),sQuery(id+"F13.wireOp",EDGE,"E7.sketch_text.stroke-33"),sQuery(id+"F13.wireOp",EDGE,"E7.sketch_text.stroke-34"),sQuery(id+"F13.wireOp",EDGE,"E7.sketch_text.stroke-35")])],"isStart":false});
            var Q3;
            Q3=makeQuery(id+"F20.opExtrude","CAP_FACE",FACE,{"disambiguationData":[OSD([sQuery(id+"F14.wireOp",EDGE,"E8.sketch_text.stroke-0"),sQuery(id+"F14.wireOp",EDGE,"E8.sketch_text.stroke-1"),sQuery(id+"F14.wireOp",EDGE,"E8.sketch_text.stroke-2"),sQuery(id+"F14.wireOp",EDGE,"E8.sketch_text.stroke-3"),sQuery(id+"F14.wireOp",EDGE,"E8.sketch_text.stroke-4"),sQuery(id+"F14.wireOp",EDGE,"E8.sketch_text.stroke-5"),sQuery(id+"F14.wireOp",EDGE,"E8.sketch_text.stroke-6"),sQuery(id+"F14.wireOp",EDGE,"E8.sketch_text.stroke-7"),sQuery(id+"F14.wireOp",EDGE,"E8.sketch_text.stroke-8"),sQuery(id+"F14.wireOp",EDGE,"E8.sketch_text.stroke-9"),sQuery(id+"F14.wireOp",EDGE,"E8.sketch_text.stroke-10"),sQuery(id+"F14.wireOp",EDGE,"E8.sketch_text.stroke-11"),sQuery(id+"F14.wireOp",EDGE,"E8.sketch_text.stroke-12"),sQuery(id+"F14.wireOp",EDGE,"E8.sketch_text.stroke-13"),sQuery(id+"F14.wireOp",EDGE,"E8.sketch_text.stroke-14"),sQuery(id+"F14.wireOp",EDGE,"E8.sketch_text.stroke-15"),sQuery(id+"F14.wireOp",EDGE,"E8.sketch_text.stroke-16"),sQuery(id+"F14.wireOp",EDGE,"E8.sketch_text.stroke-17")])],"isStart":false});
            fillet(context, id + "F23", {"entities" : qUnion([Q0, Q1, Q2, Q3]), "radius" : 0.25 * mm, "tangentPropagation" : true, "allowEdgeOverflow" : false});
        }
    });
